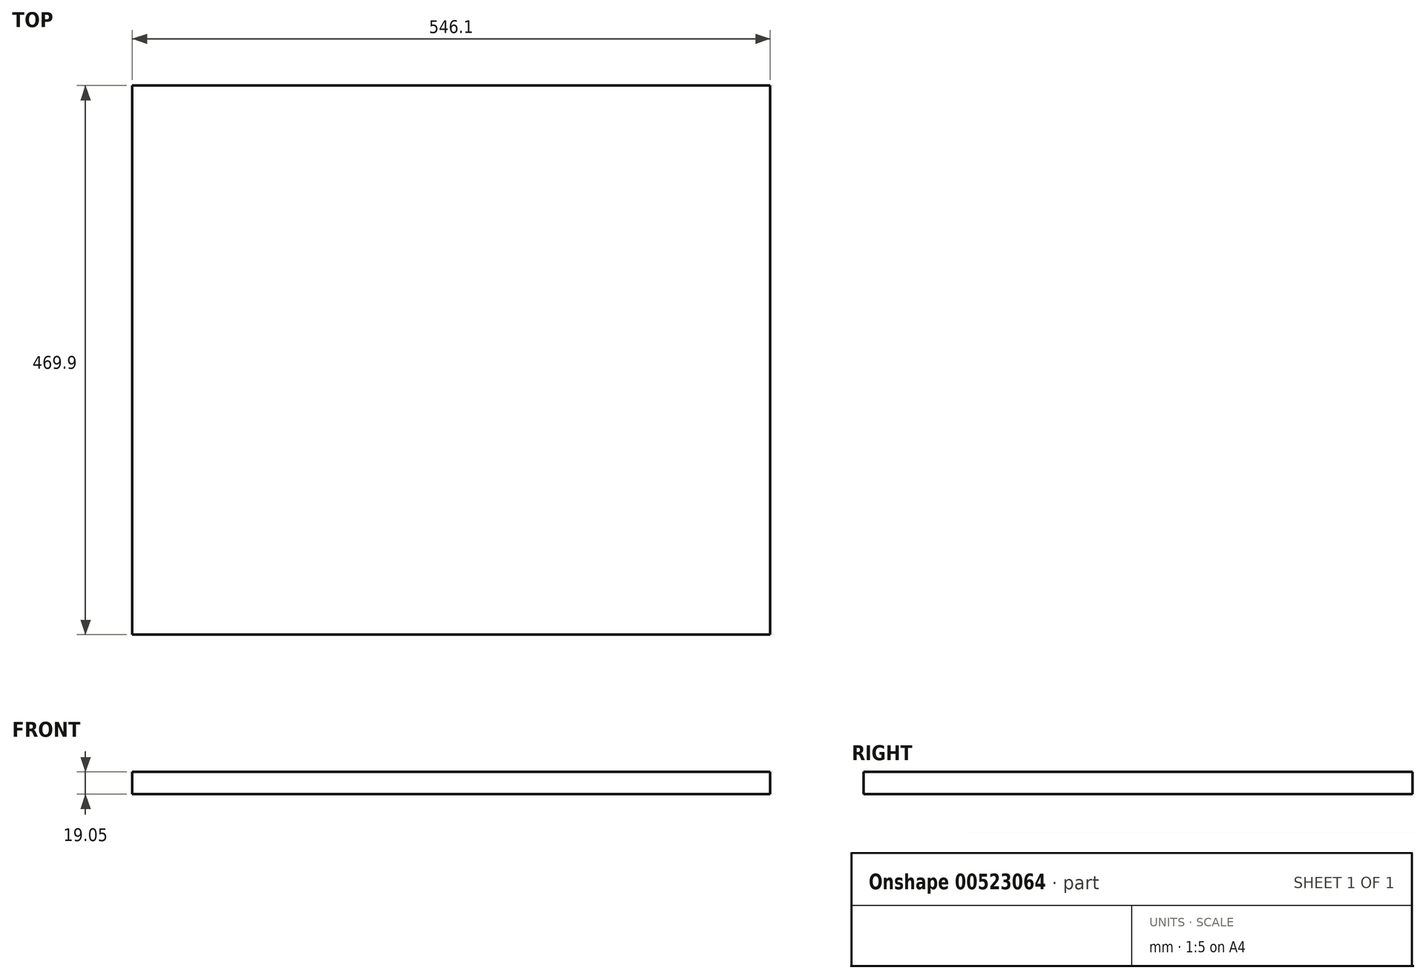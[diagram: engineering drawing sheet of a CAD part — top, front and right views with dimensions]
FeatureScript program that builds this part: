
annotation { "Feature Type Name" : "Feature", "Feature Type Description" : "" }
export const myFeature = defineFeature(function(context is Context, id is Id, definition is map)
    precondition{}
    {
        {
            var Q0;
            Q0=qCreatedBy(makeId("Top.planeOp"),FACE);
            var sketch = newSketch(context, id + "F0", { "sketchPlane" : qUnion([Q0])});
            skLineSegment(sketch, "E0.bottom", {"start": v(0, 0) * mm, "end": v(546.1, 0) * mm});
            skLineSegment(sketch, "E0.top", {"start": v(0, 469.9) * mm, "end": v(546.1, 469.9) * mm});
            skLineSegment(sketch, "E0.left", {"start": v(0, 0) * mm, "end": v(0, 469.9) * mm});
            skLineSegment(sketch, "E0.right", {"start": v(546.1, 0) * mm, "end": v(546.1, 469.9) * mm});
            skSolve(sketch);
        }
        {
            var Q0;
            Q0=qSketchRegion(id+"F0",true);
            extrude(context, id + "F1", {"entities" : qUnion([Q0]), "depth" : 19.05 * mm, "offsetDistance" : 25.4 * mm});
        }
    });
